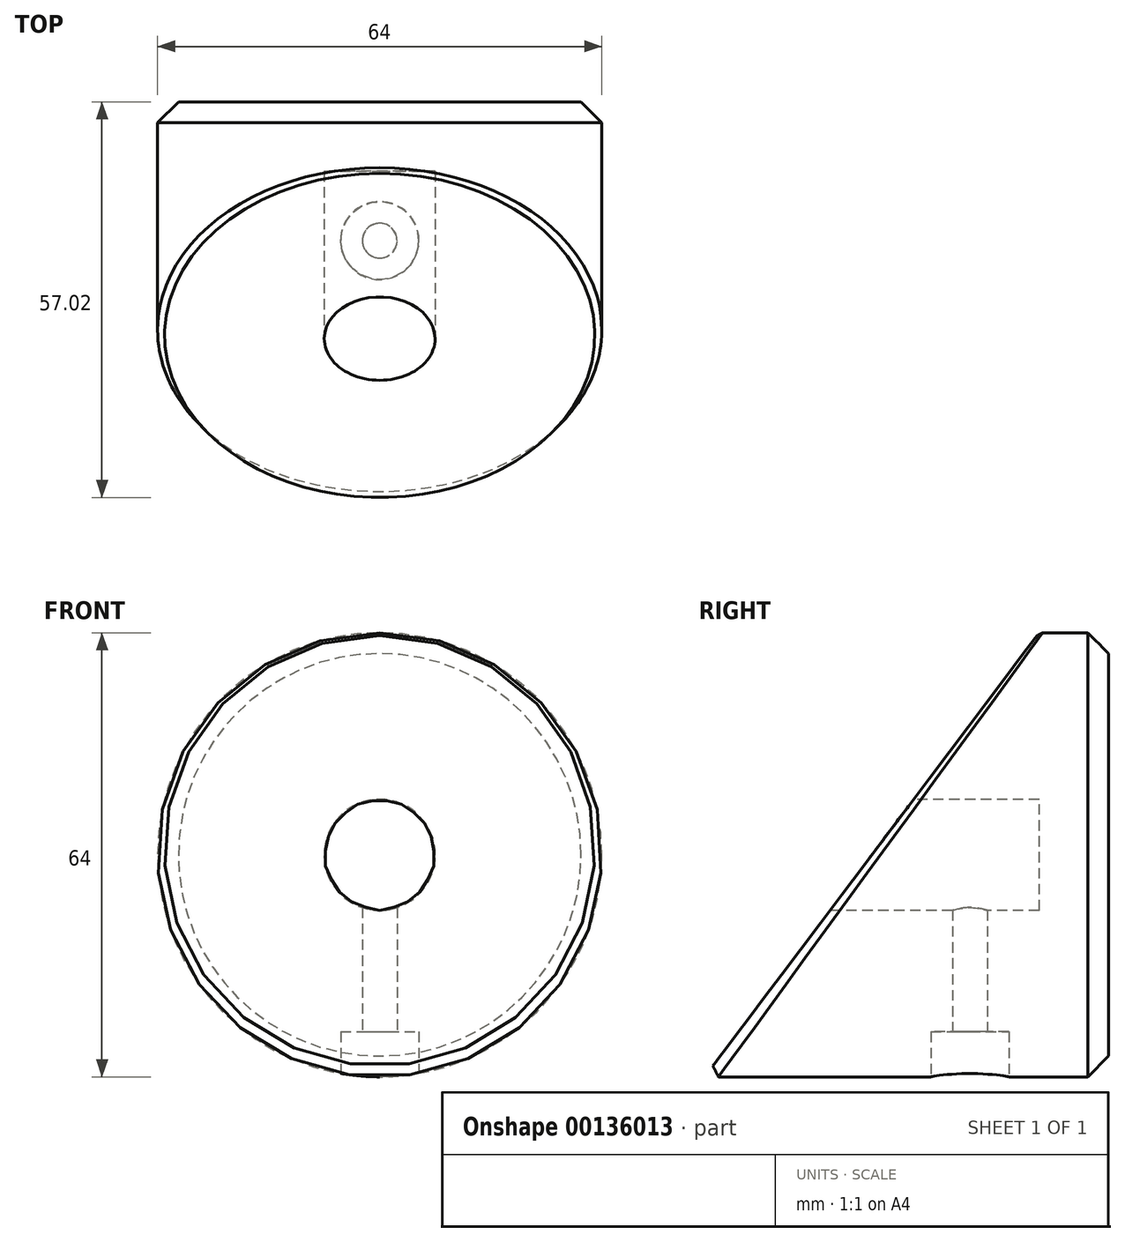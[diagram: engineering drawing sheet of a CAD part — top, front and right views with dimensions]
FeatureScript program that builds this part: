
annotation { "Feature Type Name" : "Feature", "Feature Type Description" : "" }
export const myFeature = defineFeature(function(context is Context, id is Id, definition is map)
    precondition{}
    {
        {
            var Q0;
            Q0=qCreatedBy(makeId("Front.planeOp"),FACE);
            var sketch = newSketch(context, id + "F0", { "sketchPlane" : qUnion([Q0])});
            skCircle(sketch, "E0", {"center": v(0, 0) * mm, "radius": 32 * mm});
            skSolve(sketch);
        }
        {
            var Q0;
            Q0 = qSketchRegion(id + "F0", true);
            extrude(context, id + "F1", {"entities" : qUnion([Q0]), "depth" : 50 * mm});
        }
        {
            var Q0;
            Q0=qCreatedBy(makeId("Right.planeOp"),FACE);
            var sketch = newSketch(context, id + "F2", { "sketchPlane" : qUnion([Q0])});
            skLineSegment(sketch, "E1", {"start": v(0, 0) * mm, "end": v(0, 32) * mm});
            skLineSegment(sketch, "E2", {"start": v(0, 32) * mm, "end": v(-48.23, -32) * mm});
            skLineSegment(sketch, "E3", {"start": v(-48.23, -32) * mm, "end": v(0, -32) * mm});
            skLineSegment(sketch, "E4", {"start": v(0, -32) * mm, "end": v(0, 0) * mm});
            skLineSegment(sketch, "E5.bottom", {"start": v(24.06, 45.76) * mm, "end": v(-71.93, 45.76) * mm});
            skLineSegment(sketch, "E5.top", {"start": v(24.06, -50.72) * mm, "end": v(-71.93, -50.72) * mm});
            skLineSegment(sketch, "E5.left", {"start": v(24.06, 45.76) * mm, "end": v(24.06, -50.72) * mm});
            skLineSegment(sketch, "E5.right", {"start": v(-71.93, 45.76) * mm, "end": v(-71.93, -50.72) * mm});
            skSolve(sketch);
        }
        {
            var Q0;
            Q0 = qSketchRegion(id + "F2", true);
            extrude(context, id + "F3", {"entities" : qUnion([Q0]), "operationType" : NewBodyOperationType.REMOVE, "endBound" : BoundingType.SYMMETRIC, "oppositeDirection" : true, "depth" : 80 * mm});
        }
        {
            var Q0;
            Q0=qCreatedBy(makeId("Front.planeOp"),FACE);
            cPlane(context, id + "F4", {"entities" : qUnion([Q0]), "cplaneType" : CPlaneType.OFFSET, "offset" : 80 * mm, "width" : 150 * mm, "height" : 150 * mm});
        }
        {
            var Q0;
            Q0=qCreatedBy(id+"F4.planeOp",FACE);
            var sketch = newSketch(context, id + "F5", { "sketchPlane" : qUnion([Q0])});
            skCircle(sketch, "E6", {"center": v(0, 0) * mm, "radius": 8 * mm});
            skSolve(sketch);
        }
        {
            var Q0;
            Q0 = qSketchRegion(id + "F5", true);
            extrude(context, id + "F6", {"entities" : qUnion([Q0]), "operationType" : NewBodyOperationType.REMOVE, "oppositeDirection" : true, "depth" : 80 * mm});
        }
        {
            var Q0;
            Q0=qCreatedBy(makeId("Front.planeOp"),FACE);
            var Q1;
            Q1=qCreatedBy(makeId("Front.planeOp"),FACE);
            var sketch = newSketch(context, id + "F7", { "sketchPlane" : qUnion([Q0, Q1])});
            skCircle(sketch, "E7", {"center": v(0, 0) * mm, "radius": 32 * mm});
            skSolve(sketch);
        }
        {
            var Q0;
            Q0 = qSketchRegion(id + "F7", true);
            extrude(context, id + "F8", {"entities" : qUnion([Q0]), "operationType" : NewBodyOperationType.ADD, "oppositeDirection" : true, "depth" : 5 * mm});
        }
        {
            var Q0;
            Q0=qCreatedBy(makeId("Top.planeOp"),FACE);
            cPlane(context, id + "F9", {"entities" : qUnion([Q0]), "cplaneType" : CPlaneType.OFFSET, "offset" : 32 * mm, "oppositeDirection" : true, "width" : 150 * mm, "height" : 150 * mm});
        }
        {
            var Q0;
            Q0=qCreatedBy(id+"F9.planeOp",FACE);
            var sketch = newSketch(context, id + "F10", { "sketchPlane" : qUnion([Q0])});
            skPoint(sketch, "E8", {"position": v(0, -10) * mm});
            skSolve(sketch);
        }
        {
            var Q0;
            Q0=sQuery(id+"F10.wireOp",VERTEX,"E8");
            var Q1;
            Q1=makeQuery(id+"F1.opExtrude","SWEPT_BODY",BODY,{"disambiguationData":[OSD([sQuery(id+"F0.wireOp",EDGE,"E0")])]});
            hole(context, id + "F11", {"style" : HoleStyle.C_BORE, "endStyle" : HoleEndStyle.BLIND, "oppositeDirection" : true, "standardTappedOrClearance" : lookupTablePath({ "standard" : "ISO", "size" : "5", "type" : "Drilled" }), "standardBlindInLast" : lookupTablePath({ "standard" : "ISO", "size" : "5", "type" : "Drilled" }), "holeDiameter" : 5 * mm, "cBoreDiameter" : 11.25 * mm, "cBoreDepth" : 6 * mm, "holeDepth" : 32 * mm, "locations" : qUnion([Q0]), "scope" : qUnion([Q1])});
        }
        {
            var Q0;
            Q0=makeQuery(id+"F3.boolean.opBoolean","INTERSECT",EDGE,{"derivedFrom":[makeQuery(id+"F1.opExtrude","SWEPT_FACE",FACE,{"disambiguationData":[OSD([sQuery(id+"F0.wireOp",EDGE,"E0")])]}),makeQuery(id+"F3.opExtrude","SWEPT_FACE",FACE,{"disambiguationData":[OSD([sQuery(id+"F2.wireOp",EDGE,"E2")])]})]});
            chamfer(context, id + "F12", {"entities" : qUnion([Q0]), "width" : 1 * mm, "tangentPropagation" : true});
        }
        {
            var Q0;
            Q0=makeQuery(id+"F8.opExtrude","CAP_FACE",FACE,{"disambiguationData":[OSD([sQuery(id+"F7.wireOp",EDGE,"E7")])],"isStart":false});
            var sketch = newSketch(context, id + "F13", { "sketchPlane" : qUnion([Q0])});
            skCircle(sketch, "E9.0", {"center": v(0, 0) * mm, "radius": 32 * mm});
            skSolve(sketch);
        }
        {
            var Q0;
            Q0 = qSketchRegion(id + "F13", true);
            extrude(context, id + "F14", {"entities" : qUnion([Q0]), "operationType" : NewBodyOperationType.ADD, "depth" : 5 * mm});
        }
        {
            var Q0;
            Q0=makeQuery(id+"F14.opExtrude","CAP_EDGE",EDGE,{"disambiguationData":[OSD([sQuery(id+"F13.wireOp",EDGE,"E9.0")])],"isStart":false});
            chamfer(context, id + "F15", {"entities" : qUnion([Q0]), "width" : 3 * mm, "tangentPropagation" : true});
        }
    });
